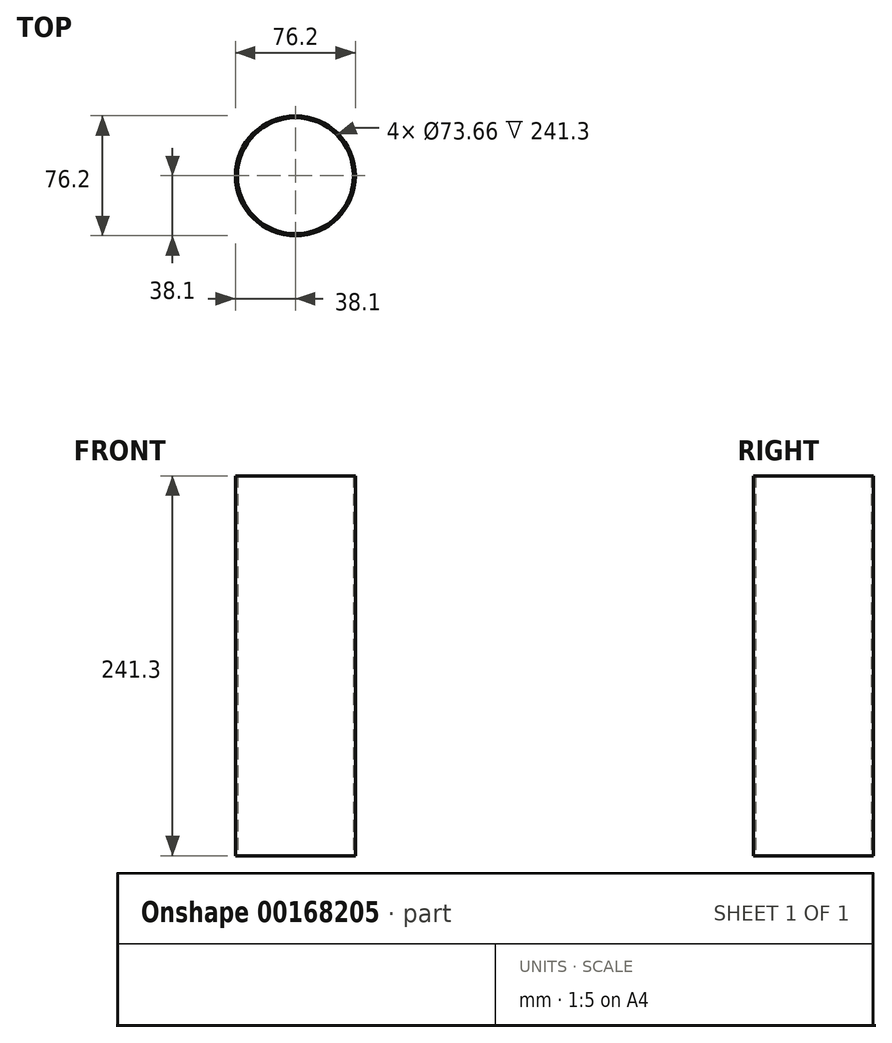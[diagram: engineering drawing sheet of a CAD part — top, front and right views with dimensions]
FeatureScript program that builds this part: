
annotation { "Feature Type Name" : "Feature", "Feature Type Description" : "" }
export const myFeature = defineFeature(function(context is Context, id is Id, definition is map)
    precondition{}
    {
        {
            var Q0;
            Q0=qCreatedBy(makeId("Top.planeOp"),FACE);
            var sketch = newSketch(context, id + "F0", { "sketchPlane" : qUnion([Q0])});
            skCircle(sketch, "E0", {"center": v(0, 0) * mm, "radius": 36.83 * mm});
            skCircle(sketch, "E1", {"center": v(0, 0) * mm, "radius": 38.1 * mm});
            skSolve(sketch);
        }
        {
            var Q0;
            Q0=qSketchRegion(id+"F0",true);
            extrude(context, id + "F1", {"entities" : qUnion([Q0]), "depth" : 241.3 * mm});
        }
    });
